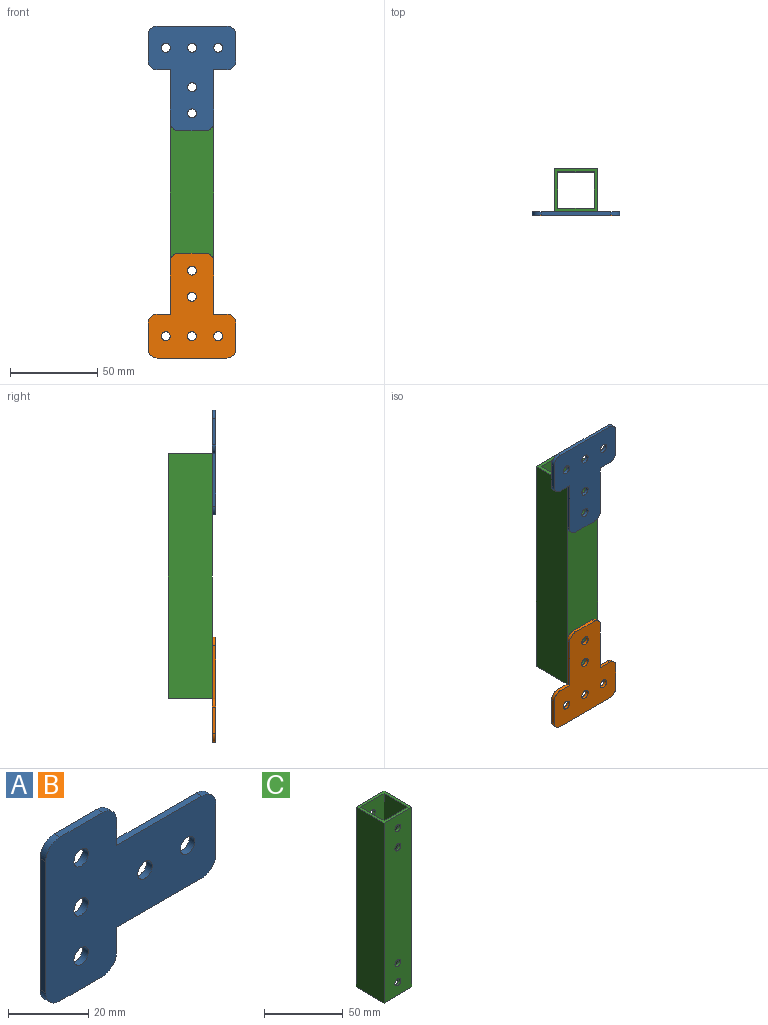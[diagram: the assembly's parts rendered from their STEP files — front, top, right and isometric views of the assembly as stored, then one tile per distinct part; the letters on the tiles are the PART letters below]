
ASSEMBLY  parts=3 mates=4
PART A: 21 faces, bbox 60x2x50 mm
  f0: plane 7.5x2mm, normal (1,0,0), area 15mm2, adj f12,f13,f14,f15
  f1: plane 15x2mm, normal (0,0,1), area 30mm2, adj f13,f14,f15,f16
  f2: plane 40x2mm, normal (-1,0,0), area 80mm2, adj f13,f14,f16,f17
  f3: plane 15x2mm, normal (0,0,-1), area 30mm2, adj f13,f14,f17,f18
  f4: plane 7.5x2mm, normal (1,0,0), area 15mm2, adj f5,f13,f14,f18
  f5: plane 30x2mm, normal (0,0,-1), area 60mm2, adj f4,f13,f14,f19
  f6: plane 15x2mm, normal (1,0,0), area 30mm2, adj f13,f14,f19,f20
  f7: cylinder r=2.55mm len=5.1mm, axis (0,1,0), area 32mm2, adj f13,f14
  f8: cylinder r=2.55mm len=5.1mm, axis (0,1,0), area 32mm2, adj f13,f14
  f9: cylinder r=2.55mm len=5.1mm, axis (0,1,0), area 32mm2, adj f13,f14
  f10: cylinder r=2.55mm len=5.1mm, axis (0,1,0), area 32mm2, adj f13,f14
  f11: cylinder r=2.55mm len=5.1mm, axis (0,1,0), area 32mm2, adj f13,f14
  f12: plane 30x2mm, normal (0,0,1), area 60mm2, adj f0,f13,f14,f20
  f13: plane 60x50mm, normal (0,-1,0), area 1990.7mm2, adj f0,f1,f2,f3,f4,f5,f6,f7
  f14: plane 60x50mm, normal (0,1,0), area 1990.7mm2, adj f0,f1,f2,f3,f4,f5,f6,f7
  f15: cylinder r=5mm len=5mm, axis (0,1,0), area 15.7mm2, adj f0,f1,f13,f14
  f16: cylinder r=5mm len=5mm, axis (0,1,0), area 15.7mm2, adj f1,f2,f13,f14
  f17: cylinder r=5mm len=5mm, axis (0,1,0), area 15.7mm2, adj f2,f3,f13,f14
  f18: cylinder r=5mm len=5mm, axis (0,1,0), area 15.7mm2, adj f3,f4,f13,f14
  f19: cylinder r=5mm len=5mm, axis (0,1,0), area 15.7mm2, adj f5,f6,f13,f14
  f20: cylinder r=5mm len=5mm, axis (0,1,0), area 15.7mm2, adj f6,f12,f13,f14
PART B: same geometry as A
PART C: 18 faces, bbox 25x25x140 mm
  f0: plane 140x21mm, normal (-1,0,0), area 2940mm2, adj f1,f7,f8,f9
  f1: plane 140x21mm, normal (0,1,0), area 2851.8mm2, adj f0,f2,f8,f9,f14,f15,f16,f17
  f2: plane 140x21mm, normal (1,0,0), area 2940mm2, adj f1,f7,f8,f9
  f3: plane 140x25mm, normal (-1,0,0), area 3500mm2, adj f4,f6,f8,f9
  f4: plane 140x25mm, normal (0,-1,0), area 3411.8mm2, adj f3,f5,f8,f9,f14,f15,f16,f17
  f5: plane 140x25mm, normal (1,0,0), area 3500mm2, adj f4,f6,f8,f9
  f6: plane 140x25mm, normal (0,1,0), area 3411.8mm2, adj f3,f5,f8,f9,f10,f11,f12,f13
  f7: plane 140x21mm, normal (0,-1,0), area 2851.8mm2, adj f0,f2,f8,f9,f10,f11,f12,f13
  f8: plane 25x25mm, normal (0,0,1), area 184mm2, adj f0,f1,f2,f3,f4,f5,f6,f7
  f9: plane 25x25mm, normal (0,0,-1), area 184mm2, adj f0,f1,f2,f3,f4,f5,f6,f7
  f10: cylinder r=2.65mm len=5.3mm, axis (0,-1,0), area 33.3mm2, adj f6,f7
  f11: cylinder r=2.65mm len=5.3mm, axis (0,-1,0), area 33.3mm2, adj f6,f7
  f12: cylinder r=2.65mm len=5.3mm, axis (0,-1,0), area 33.3mm2, adj f6,f7
  f13: cylinder r=2.65mm len=5.3mm, axis (0,-1,0), area 33.3mm2, adj f6,f7
  f14: cylinder r=2.65mm len=5.3mm, axis (0,-1,0), area 33.3mm2, adj f1,f4
  f15: cylinder r=2.65mm len=5.3mm, axis (0,-1,0), area 33.3mm2, adj f1,f4
  f16: cylinder r=2.65mm len=5.3mm, axis (0,-1,0), area 33.3mm2, adj f1,f4
  f17: cylinder r=2.65mm len=5.3mm, axis (0,-1,0), area 33.3mm2, adj f1,f4
PLACE A rot(axis=(0,1,0),90deg) t=(-37.79,-5.41,200.79)mm
PLACE B rot(axis=(0,-1,0),90deg) t=(-37.79,-5.41,60.79)mm
PLACE C rot(axis=(0,1,0),0deg) t=(-37.79,7.09,60.79)mm
MATE planar A.f13 <-> B.f13  axis (0,-1,0) through (-37.79,-7.41,200.97)mm
MATE slider B.f10 <-> C.f10  axis (0,-1,0) through (-37.79,-7.41,70.79)mm
MATE planar C.f4 <-> A.f14  axis (0,-1,0) through (-37.79,-5.41,130.79)mm
MATE slider A.f10 <-> C.f13  axis (0,-1,0) through (-37.79,-7.41,190.79)mm
